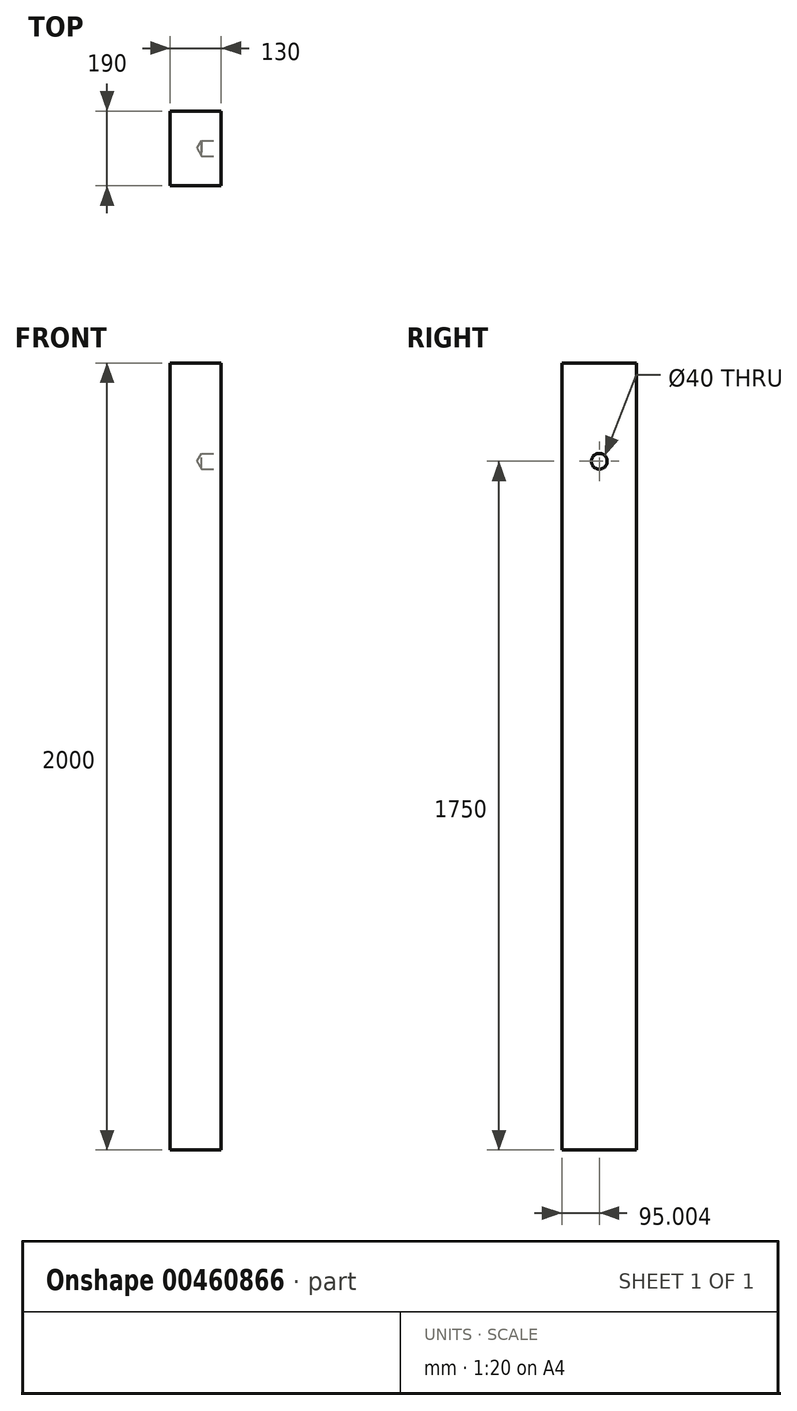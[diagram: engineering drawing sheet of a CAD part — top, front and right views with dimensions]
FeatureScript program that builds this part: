
annotation { "Feature Type Name" : "Feature", "Feature Type Description" : "" }
export const myFeature = defineFeature(function(context is Context, id is Id, definition is map)
    precondition{}
    {
        {
            var Q0;
            Q0=qCreatedBy(makeId("Top.planeOp"),FACE);
            var sketch = newSketch(context, id + "F0", { "sketchPlane" : qUnion([Q0])});
            skLineSegment(sketch, "E0.bottom", {"start": v(-65, 181.65) * mm, "end": v(65, 181.65) * mm});
            skLineSegment(sketch, "E0.top", {"start": v(-65, -8.35) * mm, "end": v(65, -8.35) * mm});
            skLineSegment(sketch, "E0.left", {"start": v(-65, 181.65) * mm, "end": v(-65, -8.35) * mm});
            skLineSegment(sketch, "E0.right", {"start": v(65, 181.65) * mm, "end": v(65, -8.35) * mm});
            skPoint(sketch, "E0.middle", {"position": v(0, 86.65) * mm});
            skLineSegment(sketch, "E1.bottom", {"start": v(34.26, 181.65) * mm, "end": v(-34.26, 181.65) * mm});
            skLineSegment(sketch, "E1.top", {"start": v(34.26, 181.65) * mm, "end": v(-34.26, 181.65) * mm});
            skLineSegment(sketch, "E1.left", {"start": v(34.26, 181.65) * mm, "end": v(34.26, 181.65) * mm});
            skLineSegment(sketch, "E1.right", {"start": v(-34.26, 181.65) * mm, "end": v(-34.26, 181.65) * mm});
            skPoint(sketch, "E1.middle", {"position": v(0, 181.65) * mm});
            skSolve(sketch);
        }
        {
            var Q0;
            Q0=makeQuery(id+"F0.imprint","IMPRINT",FACE,{"disambiguationData":[TD([[makeQuery(id+"F0.imprint","IMPRINT",EDGE,{"derivedFrom":sQuery(id+"F0.wireOp",EDGE,"E0.top")}),1.0]])]});
            extrude(context, id + "F1", {"entities" : qUnion([Q0]), "depth" : 2000 * mm});
        }
        {
            var Q0;
            Q0=makeQuery(id+"F1.opExtrude","SWEPT_FACE",FACE,{"disambiguationData":[OSD([sQuery(id+"F0.wireOp",EDGE,"E0.right")])]});
            var sketch = newSketch(context, id + "F2", { "sketchPlane" : qUnion([Q0])});
            skCircle(sketch, "E2", {"center": v(86.65, 1750) * mm, "radius": 20 * mm});
            skSolve(sketch);
        }
        {
            var Q0;
            Q0=sQuery(id+"F2.wireOp",VERTEX,"E2.center");
            var Q1;
            Q1=makeQuery(id+"F1.opExtrude","SWEPT_BODY",BODY,{"disambiguationData":[OSD([sQuery(id+"F0.wireOp",EDGE,"E0.bottom"),sQuery(id+"F0.wireOp",EDGE,"E0.top"),sQuery(id+"F0.wireOp",EDGE,"E0.left"),sQuery(id+"F0.wireOp",EDGE,"E0.right"),sQuery(id+"F0.wireOp",EDGE,"E1.top")])]});
            hole(context, id + "F3", {"style" : HoleStyle.SIMPLE, "endStyle" : HoleEndStyle.BLIND, "holeDiameter" : 40 * mm, "holeDepth" : 50 * mm, "isTappedThrough" : true, "tappedDepth" : 12 * mm, "tapClearance" : 3, "locations" : qUnion([Q0]), "scope" : qUnion([Q1])});
        }
    });
